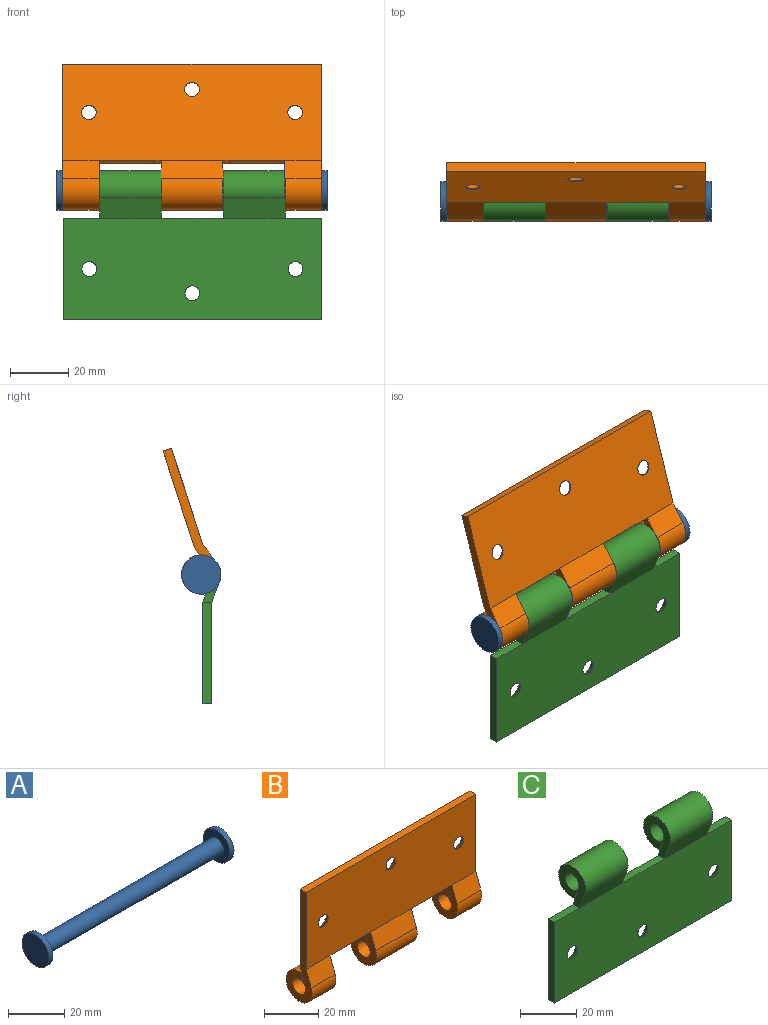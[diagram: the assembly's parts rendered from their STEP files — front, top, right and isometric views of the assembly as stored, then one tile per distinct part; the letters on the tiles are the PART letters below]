
ASSEMBLY  parts=3 mates=2
PART A: 7 faces, bbox 92.9x13.5x13.5 mm
  f0: cylinder r=6.75mm len=13.49mm, axis (1,0,0), area 85.4mm2, adj f5,f6
  f1: cylinder r=6.75mm len=13.49mm, axis (1,0,0), area 85.4mm2, adj f3,f4
  f2: cylinder r=3.37mm len=88.9mm, axis (1,0,0), area 1884.3mm2, adj f3,f5
  f3: plane 13.49x13.49mm, normal (1,0,0), area 107.3mm2, adj f1,f2
  f4: plane 13.49x13.49mm, normal (-1,0,0), area 143mm2, adj f1
  f5: plane 13.49x13.49mm, normal (-1,0,0), area 107.3mm2, adj f0,f2
  f6: plane 13.49x13.49mm, normal (1,0,0), area 143mm2, adj f0
PART B: 32 faces, bbox 88.9x13.5x51.2 mm
  f0: cone r=4.89mm half-angle=41deg, axis (0,1,0), area 83.3mm2, adj f1,f20
  f1: cylinder r=2.55mm len=5.11mm, axis (0,1,0), area 5.4mm2, adj f0,f22
  f2: cone r=4.89mm half-angle=41deg, axis (0,1,0), area 83.3mm2, adj f3,f20
  f3: cylinder r=2.55mm len=5.11mm, axis (0,1,0), area 5.4mm2, adj f2,f22
  f4: cone r=4.89mm half-angle=41deg, axis (0,1,0), area 83.3mm2, adj f5,f20
  f5: cylinder r=2.55mm len=5.11mm, axis (0,1,0), area 5.4mm2, adj f4,f22
  f6: cylinder r=3.37mm len=12.56mm, axis (-1,0,0), area 249.7mm2, adj f18,f19,f24,f28
  f7: cylinder r=6.75mm len=13.49mm, axis (-1,0,0), area 445.3mm2, adj f12,f14,f25,f29
  f8: cylinder r=3.37mm len=21.26mm, axis (-1,0,0), area 422.6mm2, adj f15,f16,f27,f30
  f9: cylinder r=6.75mm len=13.49mm, axis (-1,0,0), area 445.3mm2, adj f18,f23,f24,f28
  f10: cylinder r=6.75mm len=21.26mm, axis (-1,0,0), area 753.8mm2, adj f15,f17,f27,f30
  f11: cylinder r=3.37mm len=12.56mm, axis (-1,0,0), area 249.7mm2, adj f12,f13,f25,f29
  f12: plane 12.56x4.49mm, normal (0,-0.96,0.3), area 59mm2, adj f7,f11,f25,f29
  f13: plane 12.56x8.53mm, normal (0,0.96,-0.3), area 112.1mm2, adj f11,f20,f25,f29
  f14: plane 12.56x7.14mm, normal (0,-0.94,0.35), area 95.8mm2, adj f7,f22,f25,f29
  f15: plane 21.26x4.49mm, normal (0,-0.96,0.3), area 99.9mm2, adj f8,f10,f27,f30
  f16: plane 21.26x8.53mm, normal (0,0.96,-0.3), area 189.8mm2, adj f8,f20,f27,f30
  f17: plane 21.26x7.14mm, normal (0,-0.94,0.35), area 162.2mm2, adj f10,f22,f27,f30
  f18: plane 12.56x4.49mm, normal (0,-0.96,0.3), area 59mm2, adj f6,f9,f24,f28
  f19: plane 12.56x8.53mm, normal (0,0.96,-0.3), area 112.1mm2, adj f6,f20,f24,f28
  f20: plane 88.9x34.93mm, normal (0,1,0), area 2879.5mm2, adj f0,f2,f4,f13,f16,f19,f21,f24
  f21: plane 88.9x3.02mm, normal (0,0,1), area 268.7mm2, adj f20,f22,f24,f25
  f22: plane 88.9x34.93mm, normal (0,-1,0), area 3043.4mm2, adj f1,f3,f5,f14,f17,f21,f23,f24
  f23: plane 12.56x7.14mm, normal (0,-0.94,0.35), area 95.8mm2, adj f9,f22,f24,f28
  f24: plane 51.2x13.49mm, normal (1,0,0), area 224mm2, adj f6,f9,f18,f19,f20,f21,f22,f23
  f25: plane 51.2x13.49mm, normal (-1,0,0), area 224mm2, adj f7,f11,f12,f13,f14,f20,f21,f22
  f26: plane 21.26x3.02mm, normal (0,0,-1), area 64.3mm2, adj f20,f22,f27,f28
  f27: plane 16.27x13.49mm, normal (1,0,0), area 118.5mm2, adj f8,f10,f15,f16,f17,f26
  f28: plane 16.27x13.49mm, normal (-1,0,0), area 118.5mm2, adj f6,f9,f18,f19,f23,f26
  f29: plane 16.27x13.49mm, normal (1,0,0), area 118.5mm2, adj f7,f11,f12,f13,f14,f31
  f30: plane 16.27x13.49mm, normal (-1,0,0), area 118.5mm2, adj f8,f10,f15,f16,f17,f31
  f31: plane 21.26x3.02mm, normal (0,0,-1), area 64.3mm2, adj f20,f22,f29,f30
PART C: 28 faces, bbox 88.9x13.5x51.2 mm
  f0: cylinder r=2.55mm len=5.11mm, axis (0,1,0), area 5.4mm2, adj f1,f17
  f1: cone r=4.89mm half-angle=41deg, axis (0,1,0), area 83.3mm2, adj f0,f13
  f2: cylinder r=2.55mm len=5.11mm, axis (0,1,0), area 5.4mm2, adj f3,f17
  f3: cone r=4.89mm half-angle=41deg, axis (0,1,0), area 83.3mm2, adj f2,f13
  f4: cylinder r=2.55mm len=5.11mm, axis (0,1,0), area 5.4mm2, adj f5,f17
  f5: cone r=4.89mm half-angle=41deg, axis (0,1,0), area 83.3mm2, adj f4,f13
  f6: cylinder r=6.75mm len=21.26mm, axis (1,0,0), area 753.8mm2, adj f21,f22,f24,f25
  f7: cylinder r=3.37mm len=21.26mm, axis (1,0,0), area 422.6mm2, adj f21,f22,f23,f24
  f8: cylinder r=6.75mm len=21.26mm, axis (-1,0,0), area 753.8mm2, adj f10,f11,f15,f16
  f9: cylinder r=3.37mm len=21.26mm, axis (-1,0,0), area 422.6mm2, adj f10,f11,f14,f15
  f10: plane 16.27x13.49mm, normal (1,0,0), area 118.5mm2, adj f8,f9,f14,f15,f16,f20
  f11: plane 16.27x13.49mm, normal (-1,0,0), area 118.5mm2, adj f8,f9,f14,f15,f16,f19
  f12: plane 88.9x3.02mm, normal (0,0,-1), area 268.7mm2, adj f13,f17,f18,f26
  f13: plane 88.9x34.93mm, normal (0,1,0), area 2879.5mm2, adj f1,f3,f5,f12,f14,f18,f19,f20
  f14: plane 21.26x8.53mm, normal (0,0.96,0.3), area 189.8mm2, adj f9,f10,f11,f13
  f15: plane 21.26x4.49mm, normal (0,-0.96,-0.3), area 99.9mm2, adj f8,f9,f10,f11
  f16: plane 21.26x7.14mm, normal (0,-0.94,-0.35), area 162.2mm2, adj f8,f10,f11,f17
  f17: plane 88.9x34.93mm, normal (0,-1,0), area 3043.4mm2, adj f0,f2,f4,f12,f16,f18,f19,f20
  f18: plane 34.93x3.02mm, normal (-1,0,0), area 105.6mm2, adj f12,f13,f17,f19
  f19: plane 12.56x3.02mm, normal (0,0,1), area 38mm2, adj f11,f13,f17,f18
  f20: plane 21.26x3.02mm, normal (0,0,1), area 64.3mm2, adj f10,f13,f17,f21
  f21: plane 16.27x13.49mm, normal (-1,0,0), area 118.5mm2, adj f6,f7,f20,f23,f24,f25
  f22: plane 16.27x13.49mm, normal (1,0,0), area 118.5mm2, adj f6,f7,f23,f24,f25,f27
  f23: plane 21.26x8.53mm, normal (0,0.96,0.3), area 189.8mm2, adj f7,f13,f21,f22
  f24: plane 21.26x4.49mm, normal (0,-0.96,-0.3), area 99.9mm2, adj f6,f7,f21,f22
  f25: plane 21.26x7.14mm, normal (0,-0.94,-0.35), area 162.2mm2, adj f6,f17,f21,f22
  f26: plane 34.93x3.02mm, normal (1,0,0), area 105.6mm2, adj f12,f13,f17,f27
  f27: plane 12.56x3.02mm, normal (0,0,1), area 38mm2, adj f13,f17,f22,f26
PLACE A rot(axis=(-1,0,0),90deg) t=(10,38.13,-38.73)mm
PLACE B rot(axis=(-1,0,0),17.9deg) t=(10,38.13,-38.73)mm
PLACE C t=(10.14,38.13,-38.73)mm
MATE revolute B.f6 <-> A.f0  axis (-1,0,0) through (54.45,38.13,-38.73)mm
MATE revolute A.f0 <-> C.f8  axis (1,0,0) through (-34.45,38.13,-38.73)mm
